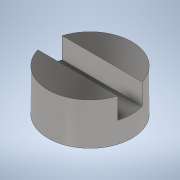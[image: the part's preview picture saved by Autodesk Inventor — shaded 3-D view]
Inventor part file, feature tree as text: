
AUTODESK INVENTOR PART (.ipt)
format: ipt  version: 2021 (Build 250183000, 183)  size: 104,960 bytes
history: native  units: mm
features: extrude x2, sketch x2
ambient origin geometry x8: Origin, YZ Plane, XZ Plane, XY Plane, X Axis, Y Axis, Z Axis, Center Point
bodies: Solid1 (feature_tree)
feature tree (4):
  extrude  "Extrusion1"  Depth=1.0mm TaperAngle=0.0deg
  extrude  "Extrusion2"  [1 undecoded]
  sketch  "Sketch1"  dims[d0=2.0mm d1=1.0mm d2=0.0mm]
  sketch  "Sketch2"  dims[d3=0.5mm d4=0.0mm]
note: 1 required parameter value undecoded (feature->parameter linkage not recoverable at this tier; creation-order binding heuristic only, values carry confidence <= 0.55)
